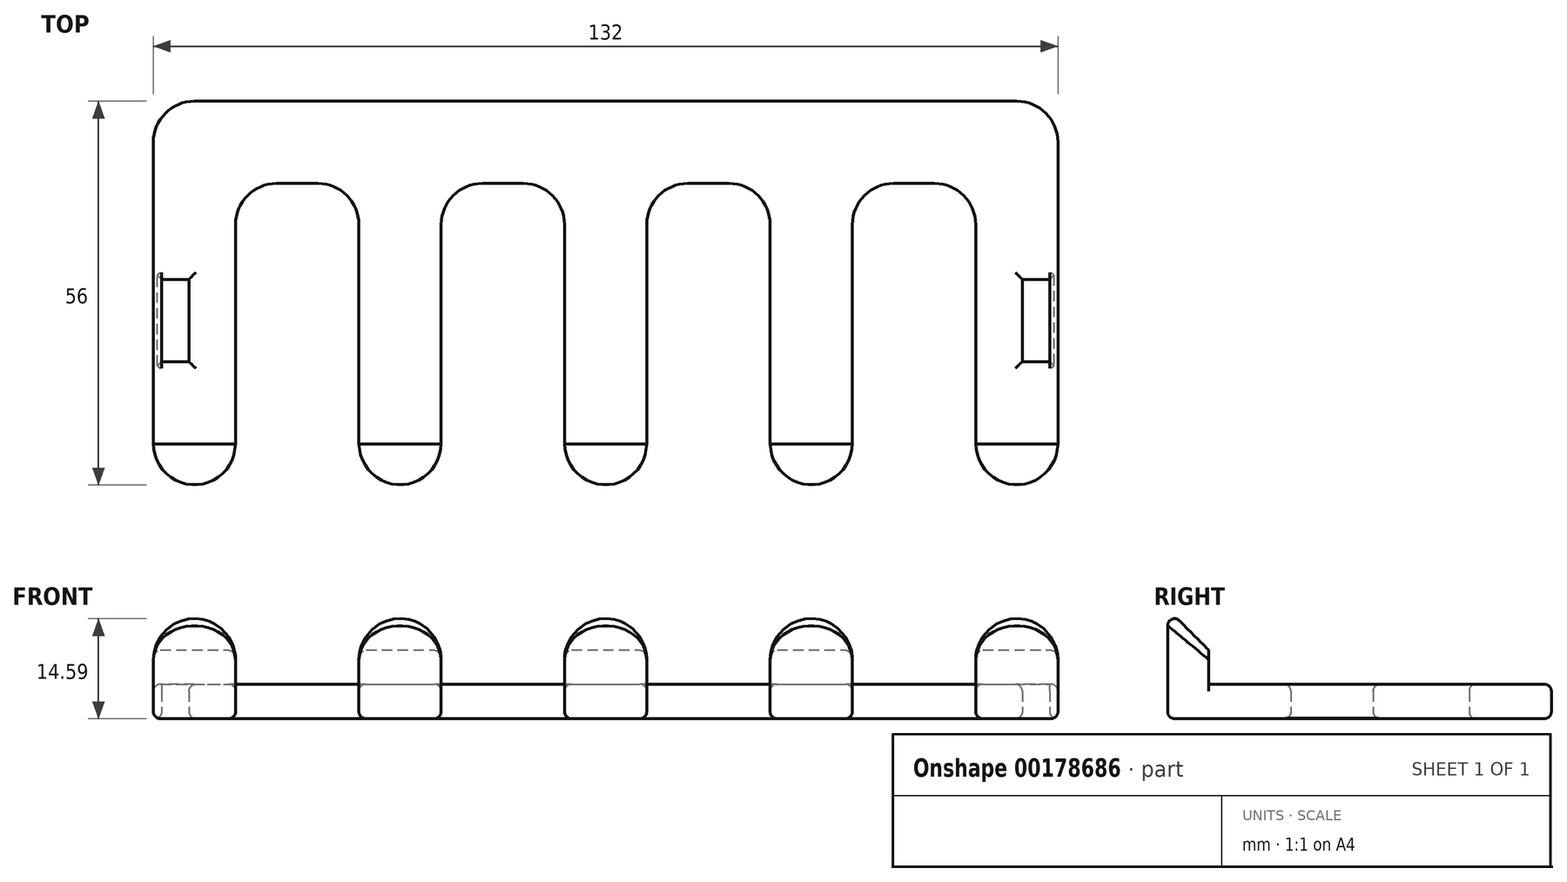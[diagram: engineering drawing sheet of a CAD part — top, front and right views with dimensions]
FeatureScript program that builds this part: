
annotation { "Feature Type Name" : "Feature", "Feature Type Description" : "" }
export const myFeature = defineFeature(function(context is Context, id is Id, definition is map)
    precondition{}
    {
        {
            var Q0;
            Q0=qCreatedBy(makeId("Top.planeOp"),FACE);
            var sketch = newSketch(context, id + "F0", { "sketchPlane" : qUnion([Q0])});
            skLineSegment(sketch, "E0.bottom", {"start": v(-66, 6) * mm, "end": v(-54, 6) * mm});
            skLineSegment(sketch, "E0.top", {"start": v(-66, 0) * mm, "end": v(-54, 0) * mm});
            skLineSegment(sketch, "E0.left", {"start": v(-66, 6) * mm, "end": v(-66, 0) * mm});
            skLineSegment(sketch, "E0.right", {"start": v(-54, 6) * mm, "end": v(-54, 0) * mm});
            skLineSegment(sketch, "E1.1.0.0", {"start": v(-36, 0) * mm, "end": v(-24, 0) * mm});
            skLineSegment(sketch, "E1.1.0.1", {"start": v(-36, 6) * mm, "end": v(-36, 0) * mm});
            skLineSegment(sketch, "E1.1.0.2", {"start": v(-24, 6) * mm, "end": v(-24, 0) * mm});
            skLineSegment(sketch, "E1.1.0.3", {"start": v(-36, 6) * mm, "end": v(-24, 6) * mm});
            skLineSegment(sketch, "E1.2.0.0", {"start": v(-6, 0) * mm, "end": v(6, 0) * mm});
            skLineSegment(sketch, "E1.2.0.1", {"start": v(-6, 6) * mm, "end": v(-6, 0) * mm});
            skLineSegment(sketch, "E1.2.0.2", {"start": v(6, 6) * mm, "end": v(6, 0) * mm});
            skLineSegment(sketch, "E1.2.0.3", {"start": v(-6, 6) * mm, "end": v(6, 6) * mm});
            skLineSegment(sketch, "E1.3.0.0", {"start": v(24, 0) * mm, "end": v(36, 0) * mm});
            skLineSegment(sketch, "E1.3.0.1", {"start": v(24, 6) * mm, "end": v(24, 0) * mm});
            skLineSegment(sketch, "E1.3.0.2", {"start": v(36, 6) * mm, "end": v(36, 0) * mm});
            skLineSegment(sketch, "E1.3.0.3", {"start": v(24, 6) * mm, "end": v(36, 6) * mm});
            skLineSegment(sketch, "E1.4.0.0", {"start": v(54, 0) * mm, "end": v(66, 0) * mm});
            skLineSegment(sketch, "E1.4.0.1", {"start": v(54, 6) * mm, "end": v(54, 0) * mm});
            skLineSegment(sketch, "E1.4.0.2", {"start": v(66, 6) * mm, "end": v(66, 0) * mm});
            skLineSegment(sketch, "E1.4.0.3", {"start": v(54, 6) * mm, "end": v(66, 6) * mm});
            skLineSegment(sketch, "E1.direction1", {"start": v(-66, 0) * mm, "end": v(-36, 0) * mm, "construction": true});
            skLineSegment(sketch, "E2", {"start": v(-66, 6) * mm, "end": v(-66, 56) * mm});
            skLineSegment(sketch, "E3", {"start": v(-66, 56) * mm, "end": v(66, 56) * mm});
            skLineSegment(sketch, "E4", {"start": v(66, 6) * mm, "end": v(66, 56) * mm});
            skLineSegment(sketch, "E5", {"start": v(-54, 44) * mm, "end": v(-36, 44) * mm});
            skLineSegment(sketch, "E6", {"start": v(-54, 6) * mm, "end": v(-54, 44) * mm});
            skLineSegment(sketch, "E7", {"start": v(-36, 6) * mm, "end": v(-36, 44) * mm});
            skLineSegment(sketch, "E8", {"start": v(-24, 6) * mm, "end": v(-24, 44) * mm});
            skLineSegment(sketch, "E9", {"start": v(-6, 6) * mm, "end": v(-6, 44) * mm});
            skLineSegment(sketch, "E10", {"start": v(6, 6) * mm, "end": v(6, 44) * mm});
            skLineSegment(sketch, "E11", {"start": v(24, 6) * mm, "end": v(24, 44) * mm});
            skLineSegment(sketch, "E12", {"start": v(36, 6) * mm, "end": v(36, 44) * mm});
            skLineSegment(sketch, "E13", {"start": v(54, 6) * mm, "end": v(54, 44) * mm});
            skLineSegment(sketch, "E14.trimOffspring", {"start": v(-24, 44) * mm, "end": v(-6, 44) * mm});
            skLineSegment(sketch, "E15.trimOffspring", {"start": v(6, 44) * mm, "end": v(24, 44) * mm});
            skLineSegment(sketch, "E16.trimOffspring", {"start": v(36, 44) * mm, "end": v(54, 44) * mm});
            skLineSegment(sketch, "E17.bottom", {"start": v(-64.8, 30) * mm, "end": v(-60.8, 30) * mm});
            skLineSegment(sketch, "E17.top", {"start": v(-64.8, 18) * mm, "end": v(-60.8, 18) * mm});
            skLineSegment(sketch, "E17.left", {"start": v(-64.8, 30) * mm, "end": v(-64.8, 18) * mm});
            skLineSegment(sketch, "E17.right", {"start": v(-60.8, 30) * mm, "end": v(-60.8, 18) * mm});
            skLineSegment(sketch, "E18.MirrorCS", {"start": v(64.8, 30) * mm, "end": v(64.8, 18) * mm});
            skLineSegment(sketch, "E19.MirrorCS", {"start": v(64.8, 18) * mm, "end": v(60.8, 18) * mm});
            skLineSegment(sketch, "E20.MirrorCS", {"start": v(60.8, 30) * mm, "end": v(60.8, 18) * mm});
            skLineSegment(sketch, "E21.MirrorCS", {"start": v(64.8, 30) * mm, "end": v(60.8, 30) * mm});
            skSolve(sketch);
        }
        {
            var Q0;
            Q0=makeQuery(id+"F0.imprint","IMPRINT",FACE,{"disambiguationData":[TD([[makeQuery(id+"F0.imprint","IMPRINT",EDGE,{"derivedFrom":sQuery(id+"F0.wireOp",EDGE,"E0.bottom")}),1.0]])]});
            extrude(context, id + "F1", {"entities" : qUnion([Q0]), "depth" : 5 * mm});
        }
        {
            var Q0;
            Q0=makeQuery(id+"F0.imprint","IMPRINT",FACE,{"disambiguationData":[TD([[makeQuery(id+"F0.imprint","IMPRINT",EDGE,{"derivedFrom":sQuery(id+"F0.wireOp",EDGE,"E0.bottom")}),-1.0]])]});
            var Q1;
            Q1=makeQuery(id+"F0.imprint","IMPRINT",FACE,{"disambiguationData":[TD([[makeQuery(id+"F0.imprint","IMPRINT",EDGE,{"derivedFrom":sQuery(id+"F0.wireOp",EDGE,"E1.1.0.0")}),1.0]])]});
            var Q2;
            Q2=makeQuery(id+"F0.imprint","IMPRINT",FACE,{"disambiguationData":[TD([[makeQuery(id+"F0.imprint","IMPRINT",EDGE,{"derivedFrom":sQuery(id+"F0.wireOp",EDGE,"E1.2.0.0")}),1.0]])]});
            var Q3;
            Q3=makeQuery(id+"F0.imprint","IMPRINT",FACE,{"disambiguationData":[TD([[makeQuery(id+"F0.imprint","IMPRINT",EDGE,{"derivedFrom":sQuery(id+"F0.wireOp",EDGE,"E1.3.0.0")}),1.0]])]});
            var Q4;
            Q4=makeQuery(id+"F0.imprint","IMPRINT",FACE,{"disambiguationData":[TD([[makeQuery(id+"F0.imprint","IMPRINT",EDGE,{"derivedFrom":sQuery(id+"F0.wireOp",EDGE,"E1.4.0.0")}),1.0]])]});
            extrude(context, id + "F2", {"entities" : qUnion([Q0, Q1, Q2, Q3, Q4]), "operationType" : NewBodyOperationType.ADD, "depth" : 16 * mm});
        }
        {
            var Q0;
            Q0=makeQuery(id+"F1.opExtrude","SWEPT_EDGE",EDGE,{"disambiguationData":[OSD([sQuery(id+"F0.wireOp",EDGE,"E2"),sQuery(id+"F0.wireOp",EDGE,"E3")])]});
            var Q1;
            Q1=makeQuery(id+"F1.opExtrude","SWEPT_EDGE",EDGE,{"disambiguationData":[OSD([sQuery(id+"F0.wireOp",EDGE,"E3"),sQuery(id+"F0.wireOp",EDGE,"E4")])]});
            var Q2;
            Q2=makeQuery(id+"F2.opExtrude","SWEPT_EDGE",EDGE,{"disambiguationData":[OSD([sQuery(id+"F0.wireOp",EDGE,"E0.top"),sQuery(id+"F0.wireOp",EDGE,"E0.left")])]});
            var Q3;
            Q3=makeQuery(id+"F2.opExtrude","SWEPT_EDGE",EDGE,{"disambiguationData":[OSD([sQuery(id+"F0.wireOp",EDGE,"E0.top"),sQuery(id+"F0.wireOp",EDGE,"E0.right")])]});
            var Q4;
            Q4=makeQuery(id+"F2.opExtrude","SWEPT_EDGE",EDGE,{"disambiguationData":[OSD([sQuery(id+"F0.wireOp",EDGE,"E1.1.0.0"),sQuery(id+"F0.wireOp",EDGE,"E1.1.0.1")])]});
            var Q5;
            Q5=makeQuery(id+"F2.opExtrude","SWEPT_EDGE",EDGE,{"disambiguationData":[OSD([sQuery(id+"F0.wireOp",EDGE,"E1.1.0.0"),sQuery(id+"F0.wireOp",EDGE,"E1.1.0.2")])]});
            var Q6;
            Q6=makeQuery(id+"F2.opExtrude","SWEPT_EDGE",EDGE,{"disambiguationData":[OSD([sQuery(id+"F0.wireOp",EDGE,"E1.2.0.0"),sQuery(id+"F0.wireOp",EDGE,"E1.2.0.1")])]});
            var Q7;
            Q7=makeQuery(id+"F2.opExtrude","SWEPT_EDGE",EDGE,{"disambiguationData":[OSD([sQuery(id+"F0.wireOp",EDGE,"E1.2.0.0"),sQuery(id+"F0.wireOp",EDGE,"E1.2.0.2")])]});
            var Q8;
            Q8=makeQuery(id+"F2.opExtrude","SWEPT_EDGE",EDGE,{"disambiguationData":[OSD([sQuery(id+"F0.wireOp",EDGE,"E1.3.0.0"),sQuery(id+"F0.wireOp",EDGE,"E1.3.0.1")])]});
            var Q9;
            Q9=makeQuery(id+"F2.opExtrude","SWEPT_EDGE",EDGE,{"disambiguationData":[OSD([sQuery(id+"F0.wireOp",EDGE,"E1.3.0.0"),sQuery(id+"F0.wireOp",EDGE,"E1.3.0.2")])]});
            var Q10;
            Q10=makeQuery(id+"F2.opExtrude","SWEPT_EDGE",EDGE,{"disambiguationData":[OSD([sQuery(id+"F0.wireOp",EDGE,"E1.4.0.0"),sQuery(id+"F0.wireOp",EDGE,"E1.4.0.1")])]});
            var Q11;
            Q11=makeQuery(id+"F2.opExtrude","SWEPT_EDGE",EDGE,{"disambiguationData":[OSD([sQuery(id+"F0.wireOp",EDGE,"E1.4.0.0"),sQuery(id+"F0.wireOp",EDGE,"E1.4.0.2")])]});
            var Q12;
            Q12=makeQuery(id+"F1.opExtrude","SWEPT_EDGE",EDGE,{"disambiguationData":[OSD([sQuery(id+"F0.wireOp",EDGE,"E5"),sQuery(id+"F0.wireOp",EDGE,"E6")])]});
            var Q13;
            Q13=makeQuery(id+"F1.opExtrude","SWEPT_EDGE",EDGE,{"disambiguationData":[OSD([sQuery(id+"F0.wireOp",EDGE,"E8"),sQuery(id+"F0.wireOp",EDGE,"E14.trimOffspring")])]});
            var Q14;
            Q14=makeQuery(id+"F1.opExtrude","SWEPT_EDGE",EDGE,{"disambiguationData":[OSD([sQuery(id+"F0.wireOp",EDGE,"E10"),sQuery(id+"F0.wireOp",EDGE,"E15.trimOffspring")])]});
            var Q15;
            Q15=makeQuery(id+"F1.opExtrude","SWEPT_EDGE",EDGE,{"disambiguationData":[OSD([sQuery(id+"F0.wireOp",EDGE,"E12"),sQuery(id+"F0.wireOp",EDGE,"E16.trimOffspring")])]});
            var Q16;
            Q16=makeQuery(id+"F1.opExtrude","SWEPT_EDGE",EDGE,{"disambiguationData":[OSD([sQuery(id+"F0.wireOp",EDGE,"E13"),sQuery(id+"F0.wireOp",EDGE,"E16.trimOffspring")])]});
            var Q17;
            Q17=makeQuery(id+"F1.opExtrude","SWEPT_EDGE",EDGE,{"disambiguationData":[OSD([sQuery(id+"F0.wireOp",EDGE,"E11"),sQuery(id+"F0.wireOp",EDGE,"E15.trimOffspring")])]});
            var Q18;
            Q18=makeQuery(id+"F1.opExtrude","SWEPT_EDGE",EDGE,{"disambiguationData":[OSD([sQuery(id+"F0.wireOp",EDGE,"E9"),sQuery(id+"F0.wireOp",EDGE,"E14.trimOffspring")])]});
            var Q19;
            Q19=makeQuery(id+"F1.opExtrude","SWEPT_EDGE",EDGE,{"disambiguationData":[OSD([sQuery(id+"F0.wireOp",EDGE,"E5"),sQuery(id+"F0.wireOp",EDGE,"E7")])]});
            fillet(context, id + "F3", {"entities" : qUnion([Q0, Q1, Q2, Q3, Q4, Q5, Q6, Q7, Q8, Q9, Q10, Q11, Q12, Q13, Q14, Q15, Q16, Q17, Q18, Q19]), "radius" : 6 * mm, "tangentPropagation" : true, "allowEdgeOverflow" : false});
        }
        {
            var Q0;
            Q0=makeQuery(id+"F2.opExtrude","CAP_EDGE",EDGE,{"disambiguationData":[OSD([sQuery(id+"F0.wireOp",EDGE,"E0.bottom")])],"isStart":false});
            var Q1;
            Q1=makeQuery(id+"F2.opExtrude","CAP_EDGE",EDGE,{"disambiguationData":[OSD([sQuery(id+"F0.wireOp",EDGE,"E1.1.0.3")])],"isStart":false});
            var Q2;
            Q2=makeQuery(id+"F2.opExtrude","CAP_EDGE",EDGE,{"disambiguationData":[OSD([sQuery(id+"F0.wireOp",EDGE,"E1.2.0.3")])],"isStart":false});
            var Q3;
            Q3=makeQuery(id+"F2.opExtrude","CAP_EDGE",EDGE,{"disambiguationData":[OSD([sQuery(id+"F0.wireOp",EDGE,"E1.3.0.3")])],"isStart":false});
            var Q4;
            Q4=makeQuery(id+"F2.opExtrude","CAP_EDGE",EDGE,{"disambiguationData":[OSD([sQuery(id+"F0.wireOp",EDGE,"E1.4.0.3")])],"isStart":false});
            chamfer(context, id + "F4", {"entities" : qUnion([Q0, Q1, Q2, Q3, Q4]), "width" : 6 * mm, "tangentPropagation" : true});
        }
        {
            var Q0;
            Q0=makeQuery(id+"F1.opExtrude","CAP_EDGE",EDGE,{"disambiguationData":[OSD([sQuery(id+"F0.wireOp",EDGE,"E3")])],"isStart":false});
            var Q1;
            {var subQ0=sQuery(id+"F0.wireOp",EDGE,"E1.4.0.3");var subQ1=sQuery(id+"F0.wireOp",EDGE,"E1.3.0.3");var subQ2=sQuery(id+"F0.wireOp",EDGE,"E1.2.0.3");var subQ3=sQuery(id+"F0.wireOp",EDGE,"E1.1.0.3");var subQ4=sQuery(id+"F0.wireOp",EDGE,"E0.bottom");Q1=makeQuery(id+"F2.boolean.opBoolean","MERGE",FACE,{"derivedFrom":[makeQuery(id+"F1.opExtrude","CAP_FACE",FACE,{"disambiguationData":[OSD([subQ4,subQ3,subQ2,subQ1,subQ0,sQuery(id+"F0.wireOp",EDGE,"E2"),sQuery(id+"F0.wireOp",EDGE,"E3"),sQuery(id+"F0.wireOp",EDGE,"E5"),sQuery(id+"F0.wireOp",EDGE,"E6"),sQuery(id+"F0.wireOp",EDGE,"E7"),sQuery(id+"F0.wireOp",EDGE,"E8"),sQuery(id+"F0.wireOp",EDGE,"E9"),sQuery(id+"F0.wireOp",EDGE,"E10"),sQuery(id+"F0.wireOp",EDGE,"E11"),sQuery(id+"F0.wireOp",EDGE,"E12"),sQuery(id+"F0.wireOp",EDGE,"E13"),sQuery(id+"F0.wireOp",EDGE,"E14.trimOffspring"),sQuery(id+"F0.wireOp",EDGE,"E15.trimOffspring"),sQuery(id+"F0.wireOp",EDGE,"E16.trimOffspring"),sQuery(id+"F0.wireOp",EDGE,"E17.bottom"),sQuery(id+"F0.wireOp",EDGE,"E17.top"),sQuery(id+"F0.wireOp",EDGE,"E17.left"),sQuery(id+"F0.wireOp",EDGE,"E17.right"),sQuery(id+"F0.wireOp",EDGE,"E18.MirrorCS"),sQuery(id+"F0.wireOp",EDGE,"E4"),sQuery(id+"F0.wireOp",EDGE,"E19.MirrorCS"),sQuery(id+"F0.wireOp",EDGE,"E20.MirrorCS"),sQuery(id+"F0.wireOp",EDGE,"E21.MirrorCS")])],"isStart":true}),makeQuery(id+"F2.opExtrude","CAP_FACE",FACE,{"disambiguationData":[OSD([subQ4,sQuery(id+"F0.wireOp",EDGE,"E0.top"),sQuery(id+"F0.wireOp",EDGE,"E0.left"),sQuery(id+"F0.wireOp",EDGE,"E0.right")])],"isStart":true}),makeQuery(id+"F2.opExtrude","CAP_FACE",FACE,{"disambiguationData":[OSD([sQuery(id+"F0.wireOp",EDGE,"E1.1.0.0"),sQuery(id+"F0.wireOp",EDGE,"E1.1.0.1"),sQuery(id+"F0.wireOp",EDGE,"E1.1.0.2"),subQ3])],"isStart":true}),makeQuery(id+"F2.opExtrude","CAP_FACE",FACE,{"disambiguationData":[OSD([sQuery(id+"F0.wireOp",EDGE,"E1.2.0.0"),sQuery(id+"F0.wireOp",EDGE,"E1.2.0.1"),sQuery(id+"F0.wireOp",EDGE,"E1.2.0.2"),subQ2])],"isStart":true}),makeQuery(id+"F2.opExtrude","CAP_FACE",FACE,{"disambiguationData":[OSD([sQuery(id+"F0.wireOp",EDGE,"E1.3.0.0"),sQuery(id+"F0.wireOp",EDGE,"E1.3.0.1"),sQuery(id+"F0.wireOp",EDGE,"E1.3.0.2"),subQ1])],"isStart":true}),makeQuery(id+"F2.opExtrude","CAP_FACE",FACE,{"disambiguationData":[OSD([sQuery(id+"F0.wireOp",EDGE,"E1.4.0.0"),sQuery(id+"F0.wireOp",EDGE,"E1.4.0.1"),sQuery(id+"F0.wireOp",EDGE,"E1.4.0.2"),subQ0])],"isStart":true})]});}
            var Q2;
            Q2=makeQuery(id+"F1.opExtrude","CAP_EDGE",EDGE,{"disambiguationData":[OSD([sQuery(id+"F0.wireOp",EDGE,"E9")])],"isStart":false});
            var Q3;
            Q3=makeQuery(id+"F1.opExtrude","CAP_EDGE",EDGE,{"disambiguationData":[OSD([sQuery(id+"F0.wireOp",EDGE,"E10")])],"isStart":false});
            var Q4;
            Q4=makeQuery(id+"F1.opExtrude","CAP_EDGE",EDGE,{"disambiguationData":[OSD([sQuery(id+"F0.wireOp",EDGE,"E7")])],"isStart":false});
            var Q5;
            Q5=makeQuery(id+"F1.opExtrude","CAP_EDGE",EDGE,{"disambiguationData":[OSD([sQuery(id+"F0.wireOp",EDGE,"E13")])],"isStart":false});
            var Q6;
            Q6=makeQuery(id+"F1.opExtrude","CAP_EDGE",EDGE,{"disambiguationData":[OSD([sQuery(id+"F0.wireOp",EDGE,"E17.right")])],"isStart":false});
            var Q7;
            Q7=makeQuery(id+"F1.opExtrude","CAP_EDGE",EDGE,{"disambiguationData":[OSD([sQuery(id+"F0.wireOp",EDGE,"E17.top")])],"isStart":false});
            var Q8;
            Q8=makeQuery(id+"F1.opExtrude","CAP_EDGE",EDGE,{"disambiguationData":[OSD([sQuery(id+"F0.wireOp",EDGE,"E17.bottom")])],"isStart":false});
            var Q9;
            Q9=makeQuery(id+"F1.opExtrude","CAP_EDGE",EDGE,{"disambiguationData":[OSD([sQuery(id+"F0.wireOp",EDGE,"E19.MirrorCS")])],"isStart":false});
            var Q10;
            Q10=makeQuery(id+"F1.opExtrude","CAP_EDGE",EDGE,{"disambiguationData":[OSD([sQuery(id+"F0.wireOp",EDGE,"E20.MirrorCS")])],"isStart":false});
            var Q11;
            Q11=makeQuery(id+"F1.opExtrude","CAP_EDGE",EDGE,{"disambiguationData":[OSD([sQuery(id+"F0.wireOp",EDGE,"E21.MirrorCS")])],"isStart":false});
            var Q12;
            Q12=makeQuery(id+"F4.opChamfer","BLEND_EDGE",EDGE,{"blendedFrom":[makeQuery(id+"F2.opExtrude","CAP_EDGE",EDGE,{"disambiguationData":[OSD([sQuery(id+"F0.wireOp",EDGE,"E1.1.0.3")])],"isStart":false}),makeQuery(id+"F3.opFillet","BLEND_FACE",FACE,{"disambiguationData":[OSD([sQuery(id+"F0.wireOp",EDGE,"E1.1.0.0"),sQuery(id+"F0.wireOp",EDGE,"E1.1.0.1")])]})],"blendedInto":[makeQuery(id+"F3.opFillet","BLEND_FACE",FACE,{"disambiguationData":[OSD([sQuery(id+"F0.wireOp",EDGE,"E1.1.0.0"),sQuery(id+"F0.wireOp",EDGE,"E1.1.0.1")])]})]});
            var Q13;
            Q13=makeQuery(id+"F4.opChamfer","BLEND_EDGE",EDGE,{"blendedFrom":[makeQuery(id+"F2.opExtrude","CAP_EDGE",EDGE,{"disambiguationData":[OSD([sQuery(id+"F0.wireOp",EDGE,"E0.bottom")])],"isStart":false}),makeQuery(id+"F3.opFillet","BLEND_FACE",FACE,{"disambiguationData":[OSD([sQuery(id+"F0.wireOp",EDGE,"E0.top"),sQuery(id+"F0.wireOp",EDGE,"E0.left")])]})],"blendedInto":[makeQuery(id+"F3.opFillet","BLEND_FACE",FACE,{"disambiguationData":[OSD([sQuery(id+"F0.wireOp",EDGE,"E0.top"),sQuery(id+"F0.wireOp",EDGE,"E0.left")])]})]});
            var Q14;
            Q14=makeQuery(id+"F4.opChamfer","BLEND_EDGE",EDGE,{"blendedFrom":[makeQuery(id+"F2.opExtrude","CAP_EDGE",EDGE,{"disambiguationData":[OSD([sQuery(id+"F0.wireOp",EDGE,"E1.2.0.3")])],"isStart":false}),makeQuery(id+"F3.opFillet","BLEND_FACE",FACE,{"disambiguationData":[OSD([sQuery(id+"F0.wireOp",EDGE,"E1.2.0.0"),sQuery(id+"F0.wireOp",EDGE,"E1.2.0.1")])]})],"blendedInto":[makeQuery(id+"F3.opFillet","BLEND_FACE",FACE,{"disambiguationData":[OSD([sQuery(id+"F0.wireOp",EDGE,"E1.2.0.0"),sQuery(id+"F0.wireOp",EDGE,"E1.2.0.1")])]})]});
            var Q15;
            Q15=makeQuery(id+"F4.opChamfer","BLEND_EDGE",EDGE,{"blendedFrom":[makeQuery(id+"F2.opExtrude","CAP_EDGE",EDGE,{"disambiguationData":[OSD([sQuery(id+"F0.wireOp",EDGE,"E1.3.0.3")])],"isStart":false}),makeQuery(id+"F3.opFillet","BLEND_FACE",FACE,{"disambiguationData":[OSD([sQuery(id+"F0.wireOp",EDGE,"E1.3.0.0"),sQuery(id+"F0.wireOp",EDGE,"E1.3.0.1")])]})],"blendedInto":[makeQuery(id+"F3.opFillet","BLEND_FACE",FACE,{"disambiguationData":[OSD([sQuery(id+"F0.wireOp",EDGE,"E1.3.0.0"),sQuery(id+"F0.wireOp",EDGE,"E1.3.0.1")])]})]});
            var Q16;
            Q16=makeQuery(id+"F4.opChamfer","BLEND_EDGE",EDGE,{"blendedFrom":[makeQuery(id+"F2.opExtrude","CAP_EDGE",EDGE,{"disambiguationData":[OSD([sQuery(id+"F0.wireOp",EDGE,"E1.4.0.3")])],"isStart":false}),makeQuery(id+"F3.opFillet","BLEND_FACE",FACE,{"disambiguationData":[OSD([sQuery(id+"F0.wireOp",EDGE,"E1.4.0.0"),sQuery(id+"F0.wireOp",EDGE,"E1.4.0.1")])]})],"blendedInto":[makeQuery(id+"F3.opFillet","BLEND_FACE",FACE,{"disambiguationData":[OSD([sQuery(id+"F0.wireOp",EDGE,"E1.4.0.0"),sQuery(id+"F0.wireOp",EDGE,"E1.4.0.1")])]})]});
            fillet(context, id + "F5", {"entities" : qUnion([Q0, Q1, Q2, Q3, Q4, Q5, Q6, Q7, Q8, Q9, Q10, Q11, Q12, Q13, Q14, Q15, Q16]), "tangentPropagation" : true, "radius" : 1 * mm, "defaultsChanged" : false, "vertexSettings" : [], "allowEdgeOverflow" : false});
        }
    });
